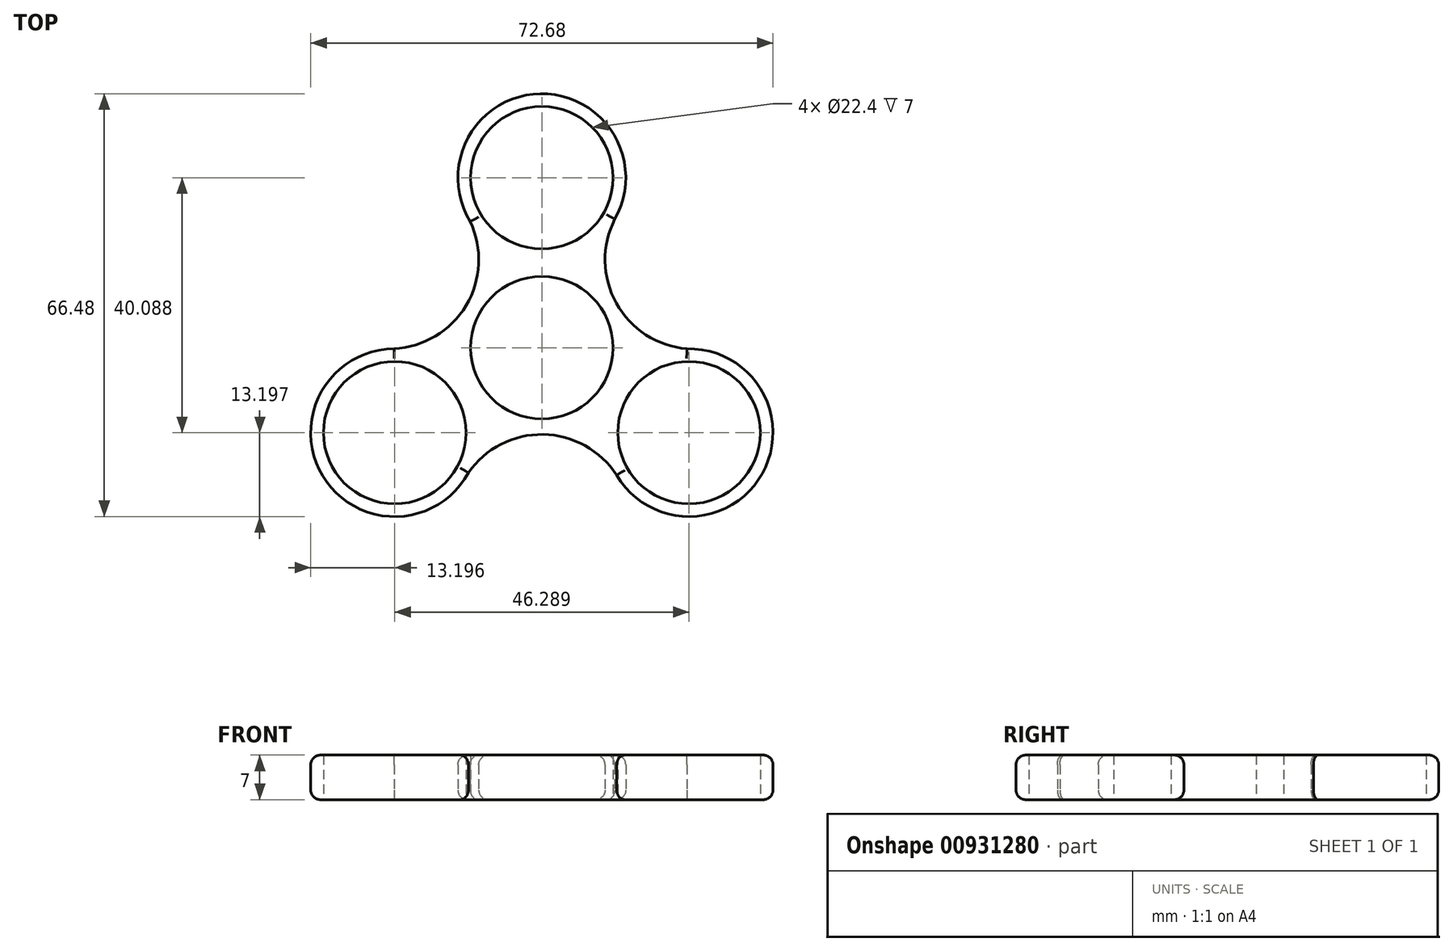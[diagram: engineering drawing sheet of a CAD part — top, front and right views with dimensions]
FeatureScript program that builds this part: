
annotation { "Feature Type Name" : "Feature", "Feature Type Description" : "" }
export const myFeature = defineFeature(function(context is Context, id is Id, definition is map)
    precondition{}
    {
        {
            var Q0;
            Q0=qCreatedBy(makeId("Top.planeOp"),FACE);
            var sketch = newSketch(context, id + "F0", { "sketchPlane" : qUnion([Q0])});
            skCircle(sketch, "E0", {"center": v(0, 0) * mm, "radius": 11.2 * mm});
            skCircle(sketch, "E1", {"center": v(0, 26.72) * mm, "radius": 11.2 * mm});
            skArc(sketch, "E2", {"start": v(11.48, 20.22) * mm, "mid": v(-0.22, 39.92) * mm, "end": v(-11.26, 19.84) * mm});
            skCircle(sketch, "E3.1.0", {"center": v(-23.14, -13.36) * mm, "radius": 11.2 * mm});
            skArc(sketch, "E3.1.1", {"start": v(-23.25, -0.16) * mm, "mid": v(-34.47, -20.15) * mm, "end": v(-11.55, -19.67) * mm});
            skCircle(sketch, "E3.2.0", {"center": v(23.14, -13.36) * mm, "radius": 11.2 * mm});
            skArc(sketch, "E3.2.1", {"start": v(11.77, -20.05) * mm, "mid": v(34.68, -19.77) * mm, "end": v(22.81, -0.17) * mm});
            skLineSegment(sketch, "E4", {"start": v(-23.14, -13.36) * mm, "end": v(-13.52, -7.63) * mm, "construction": true});
            skArc(sketch, "E5", {"start": v(11.48, 20.22) * mm, "mid": v(11.7, 7) * mm, "end": v(22.81, -0.17) * mm});
            skArc(sketch, "E6.1.0", {"start": v(-23.25, -0.16) * mm, "mid": v(-11.92, 6.64) * mm, "end": v(-11.26, 19.84) * mm});
            skArc(sketch, "E6.2.0", {"start": v(11.77, -20.05) * mm, "mid": v(0.2, -13.64) * mm, "end": v(-11.55, -19.67) * mm});
            skLineSegment(sketch, "E7.trimOffspring", {"start": v(9.42, 6.06) * mm, "end": v(11.54, 7.32) * mm, "construction": true});
            skSolve(sketch);
        }
        {
            var Q0;
            Q0=makeQuery(id+"F0.imprint","IMPRINT",FACE,{"disambiguationData":[TD([[makeQuery(id+"F0.imprint","IMPRINT",EDGE,{"derivedFrom":sQuery(id+"F0.wireOp",EDGE,"E0")}),-1.0]])]});
            extrude(context, id + "F1", {"entities" : qUnion([Q0]), "depth" : 7 * mm, "offsetDistance" : 25 * mm});
        }
        {
            var Q0;
            Q0=makeQuery(id+"F1.opExtrude","CAP_EDGE",EDGE,{"disambiguationData":[OSD([sQuery(id+"F0.wireOp",EDGE,"E6.2.0")])],"isStart":false});
            var Q1;
            Q1=makeQuery(id+"F1.opExtrude","CAP_EDGE",EDGE,{"disambiguationData":[OSD([sQuery(id+"F0.wireOp",EDGE,"E3.1.1")])],"isStart":false});
            var Q2;
            Q2=makeQuery(id+"F1.opExtrude","CAP_EDGE",EDGE,{"disambiguationData":[OSD([sQuery(id+"F0.wireOp",EDGE,"E6.1.0")])],"isStart":false});
            var Q3;
            Q3=makeQuery(id+"F1.opExtrude","CAP_EDGE",EDGE,{"disambiguationData":[OSD([sQuery(id+"F0.wireOp",EDGE,"E2")])],"isStart":false});
            var Q4;
            Q4=makeQuery(id+"F1.opExtrude","CAP_EDGE",EDGE,{"disambiguationData":[OSD([sQuery(id+"F0.wireOp",EDGE,"E5")])],"isStart":false});
            var Q5;
            Q5=makeQuery(id+"F1.opExtrude","CAP_EDGE",EDGE,{"disambiguationData":[OSD([sQuery(id+"F0.wireOp",EDGE,"E3.2.1")])],"isStart":false});
            fillet(context, id + "F2", {"entities" : qUnion([Q0, Q1, Q2, Q3, Q4, Q5]), "radius" : 1.5 * mm, "tangentPropagation" : true, "allowEdgeOverflow" : false});
        }
        {
            var Q0;
            Q0=makeQuery(id+"F1.opExtrude","CAP_EDGE",EDGE,{"disambiguationData":[OSD([sQuery(id+"F0.wireOp",EDGE,"E3.2.1")])],"isStart":true});
            var Q1;
            Q1=makeQuery(id+"F1.opExtrude","CAP_EDGE",EDGE,{"disambiguationData":[OSD([sQuery(id+"F0.wireOp",EDGE,"E5")])],"isStart":true});
            var Q2;
            Q2=makeQuery(id+"F1.opExtrude","CAP_EDGE",EDGE,{"disambiguationData":[OSD([sQuery(id+"F0.wireOp",EDGE,"E2")])],"isStart":true});
            var Q3;
            Q3=makeQuery(id+"F1.opExtrude","CAP_EDGE",EDGE,{"disambiguationData":[OSD([sQuery(id+"F0.wireOp",EDGE,"E6.1.0")])],"isStart":true});
            var Q4;
            Q4=makeQuery(id+"F1.opExtrude","CAP_EDGE",EDGE,{"disambiguationData":[OSD([sQuery(id+"F0.wireOp",EDGE,"E3.1.1")])],"isStart":true});
            var Q5;
            Q5=makeQuery(id+"F1.opExtrude","CAP_EDGE",EDGE,{"disambiguationData":[OSD([sQuery(id+"F0.wireOp",EDGE,"E6.2.0")])],"isStart":true});
            fillet(context, id + "F3", {"entities" : qUnion([Q0, Q1, Q2, Q3, Q4, Q5]), "radius" : 1.5 * mm, "tangentPropagation" : true, "allowEdgeOverflow" : false});
        }
    });
